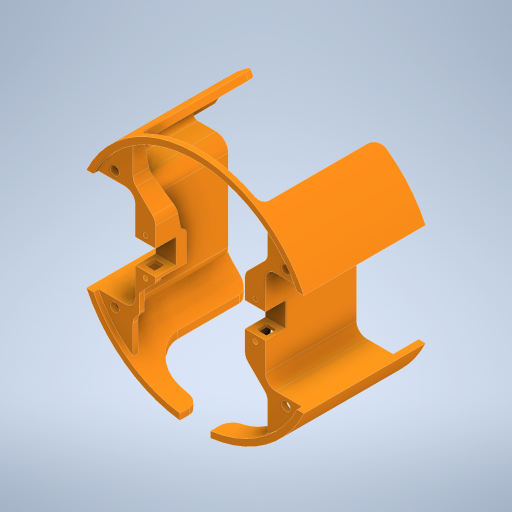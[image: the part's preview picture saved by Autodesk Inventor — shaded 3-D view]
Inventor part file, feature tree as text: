
AUTODESK INVENTOR PART (.ipt)
format: ipt  version: 2023.1 (Build 271208000, 208)  size: 842,752 bytes
history: native  units: mm
features: extrude x13, sketch x10, fillet x7, chamfer x4, projected_geometry x4, other x1
ambient origin geometry x8: Origin, YZ Plane, XZ Plane, XY Plane, X Axis, Y Axis, Z Axis, Center Point
bodies: Body1 (feature_tree)
feature tree (39):
  other  "Sólido1"
  extrude  "Extrusión1"  Depth=3.0mm
  extrude  "Extrusión2"  Depth=18.0mm
  extrude  "Extrusión3"  Depth=9.0mm
  fillet  "Empalme12"  Radius=15.0mm
  extrude  "Extrusión20"  Depth=60.0mm
  extrude  "Extrusión21"  Depth=7.0mm TaperAngle=0.0deg
  sketch  "Boceto16"  dims[d3=50.0mm d4=18.0mm]
  extrude  "Extrusión22"  Depth=5.0mm
  chamfer  "Chaflán3"  Distance=83.82mm
  chamfer  "Chaflán4"  Distance=26.04mm
  extrude  "Extrusión24"  Depth=5.0mm
  extrude  "Extrusión25"  TaperAngle=0.0deg  [1 undecoded]
  sketch  "Boceto19"  dims[d13=2.5mm d14=0.0mm d15=7.0mm d16=0.0mm]
  extrude  "Extrusión26"  Depth=10.0mm
  extrude  "Extrusión28"  Depth=5.0mm
  extrude  "Extrusión29"  Depth=5.0mm
  sketch  "Boceto23"  dims[d116=110.0mm]
  sketch  "Boceto24"  dims[d117=41.91mm]
  extrude  "Extrusión30"  Depth=5.0mm
  extrude  "Extrusión31"  Depth=5.0mm
  sketch  "Boceto25"  dims[d119=57.92mm d120=83.82mm d121=26.04mm d131=1.079663mm d132=0.0mm d133=10.0mm d134=2.5mm d135=18.0mm d136=12.15mm d137=18.0mm d138=1.5mm d139=1.5mm d140=5.0mm d141=10.0mm d142=0.0mm d151=5.0mm d152=0.0mm d154=4.25mm d155=4.25mm d156=1.0mm d157=3.0mm d158=0.0mm d159=10.0mm d160=15.0mm d161=45.0deg d162=7.0mm d163=35.0mm d164=45.0deg d180=5.0mm d181=5.0mm d182=1.0mm d183=0.0mm d184=5.0mm d185=5.0mm d186=10.0mm d187=0.0mm d188=4.25mm d189=5.0mm d190=5.0mm d191=20.0mm d192=5.0mm d193=0.0mm d194=0.0mm d197=50.0mm d198=0.0mm d199=42.0mm d200=0.0mm d201=1.0mm d202=1.0mm d203=35.0mm d204=0.0mm d205=1.0mm d206=1.0mm d207=10.0mm d208=0.0mm d209=2.0mm d210=1.0mm d211=2.0mm d212=2.0mm d213=7.0mm d214=35.0mm d215=45.0deg d216=3.5mm d217=7.0mm d218=35.0mm d219=45.0deg d220=3.5mm d221=15.0mm d222=5.0mm d42=0.5mm d43=0.872665mm d44=0.5mm d45=0.872665mm d125=0.5mm d126=0.872665mm d127=0.5mm d128=0.872665mm]
  fillet  "Empalme17"  Radius=1.5mm
  fillet  "Empalme18"  Radius=1.5mm
  chamfer  "Chaflán9"  Distance=5.0mm
  fillet  "Empalme19"  Radius=10.0mm
  chamfer  "Chaflán10"  Distance=5.0mm
  fillet  "Empalme20"  Radius=4.25mm
  fillet  "Empalme21"  Radius=4.25mm
  fillet  "Empalme22"  Radius=1.0mm
  sketch  "Boceto15"  dims[d0=111.5mm d1=3.0mm]
  projected_geometry  "Contorno proyectado16"
  projected_geometry  "Contorno proyectado17"
  projected_geometry  "Contorno proyectado18"
  projected_geometry  "Contorno proyectado19"
  sketch  "Boceto17"  dims[d5=4.5mm d8=9.0mm d9=15.0mm]
  sketch  "Boceto18"  dims[d10=2.5mm d11=0.0mm d12=60.0mm]
  sketch  "Boceto20"  dims[d24=20.0mm d28=5.0mm]
  sketch  "Boceto22"  dims[d76=0.5mm]
note: 1 required parameter value undecoded (feature->parameter linkage not recoverable at this tier; creation-order binding heuristic only, values carry confidence <= 0.55)
